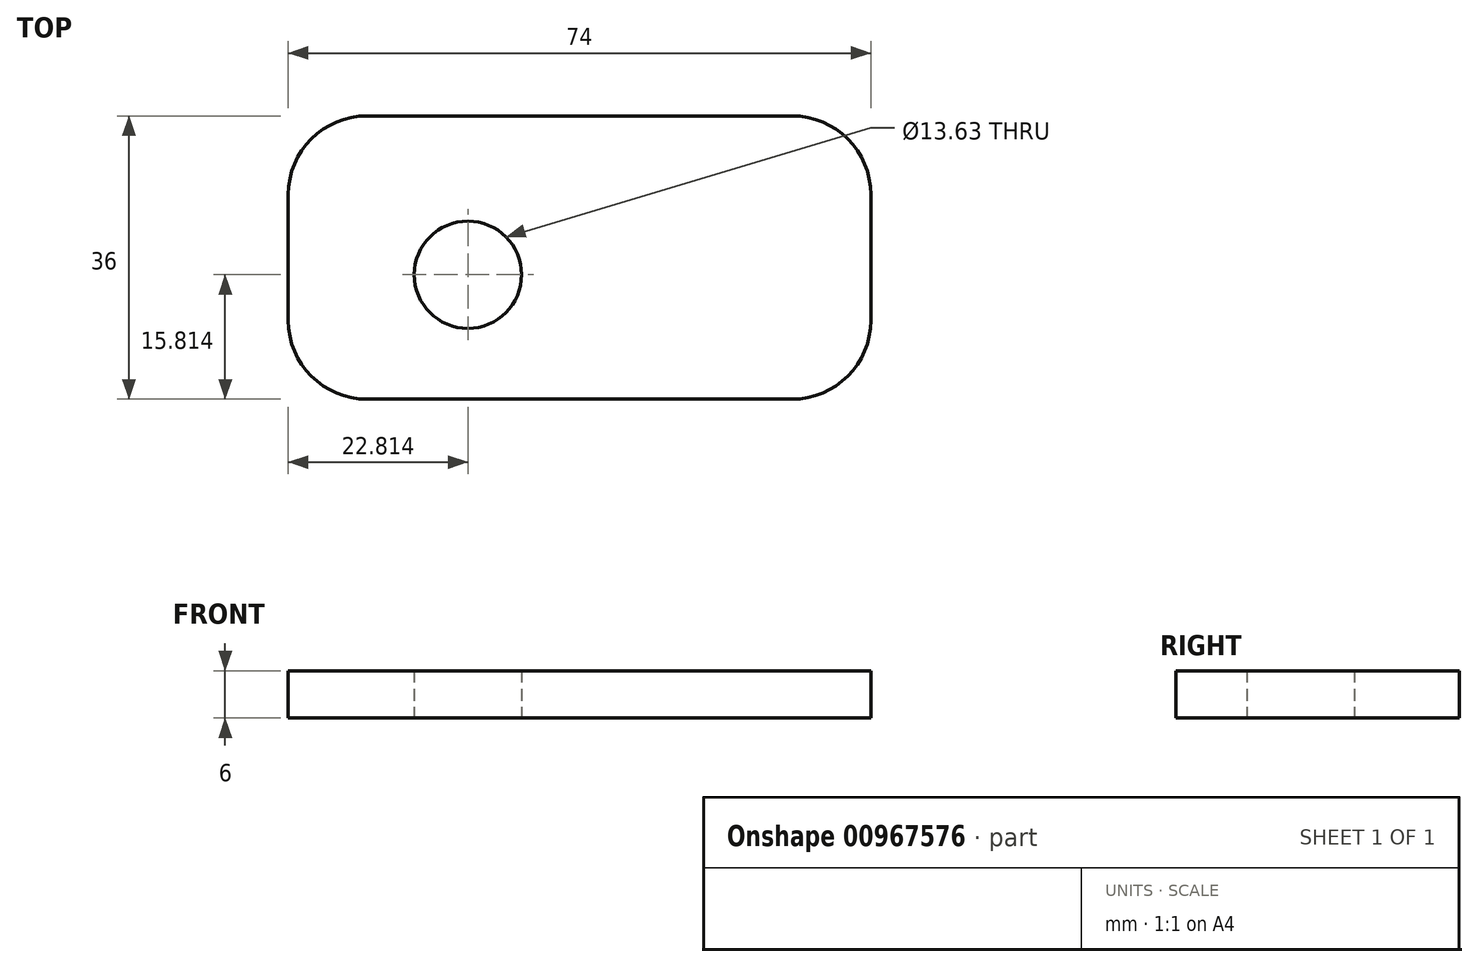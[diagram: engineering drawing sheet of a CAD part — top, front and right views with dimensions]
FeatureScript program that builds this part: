
annotation { "Feature Type Name" : "Feature", "Feature Type Description" : "" }
export const myFeature = defineFeature(function(context is Context, id is Id, definition is map)
    precondition{}
    {
        {
            var Q0;
            Q0=qCreatedBy(makeId("Top.planeOp"),FACE);
            var sketch = newSketch(context, id + "F0", { "sketchPlane" : qUnion([Q0])});
            skLineSegment(sketch, "E0.bottom", {"start": v(27, 18) * mm, "end": v(-27, 18) * mm});
            skLineSegment(sketch, "E0.top", {"start": v(27, -18) * mm, "end": v(-27, -18) * mm});
            skLineSegment(sketch, "E0.left", {"start": v(37, 8) * mm, "end": v(37, -8) * mm});
            skLineSegment(sketch, "E0.right", {"start": v(-37, 8) * mm, "end": v(-37, -8) * mm});
            skPoint(sketch, "E0.middle", {"position": v(0, 0) * mm});
            skPoint(sketch, "E1.visualSharp", {"position": v(-37, 18) * mm});
            skArc(sketch, "E1.filletArc", {"start": v(-27, 18) * mm, "mid": v(-34.07, 15.07) * mm, "end": v(-37, 8) * mm});
            skPoint(sketch, "E2.visualSharp", {"position": v(-37, -18) * mm});
            skArc(sketch, "E2.filletArc", {"start": v(-37, -8) * mm, "mid": v(-34.07, -15.07) * mm, "end": v(-27, -18) * mm});
            skPoint(sketch, "E3.visualSharp", {"position": v(37, -18) * mm});
            skArc(sketch, "E3.filletArc", {"start": v(27, -18) * mm, "mid": v(34.07, -15.07) * mm, "end": v(37, -8) * mm});
            skPoint(sketch, "E4.visualSharp", {"position": v(37, 18) * mm});
            skArc(sketch, "E4.filletArc", {"start": v(37, 8) * mm, "mid": v(34.07, 15.07) * mm, "end": v(27, 18) * mm});
            skCircle(sketch, "E5", {"center": v(-14.19, -2.19) * mm, "radius": 6.81 * mm});
            skSolve(sketch);
        }
        {
            var Q0;
            Q0 = qSketchRegion(id + "F0", true);
            extrude(context, id + "F1", {"entities" : qUnion([Q0]), "depth" : 6 * mm, "offsetDistance" : 25 * mm});
        }
    });
